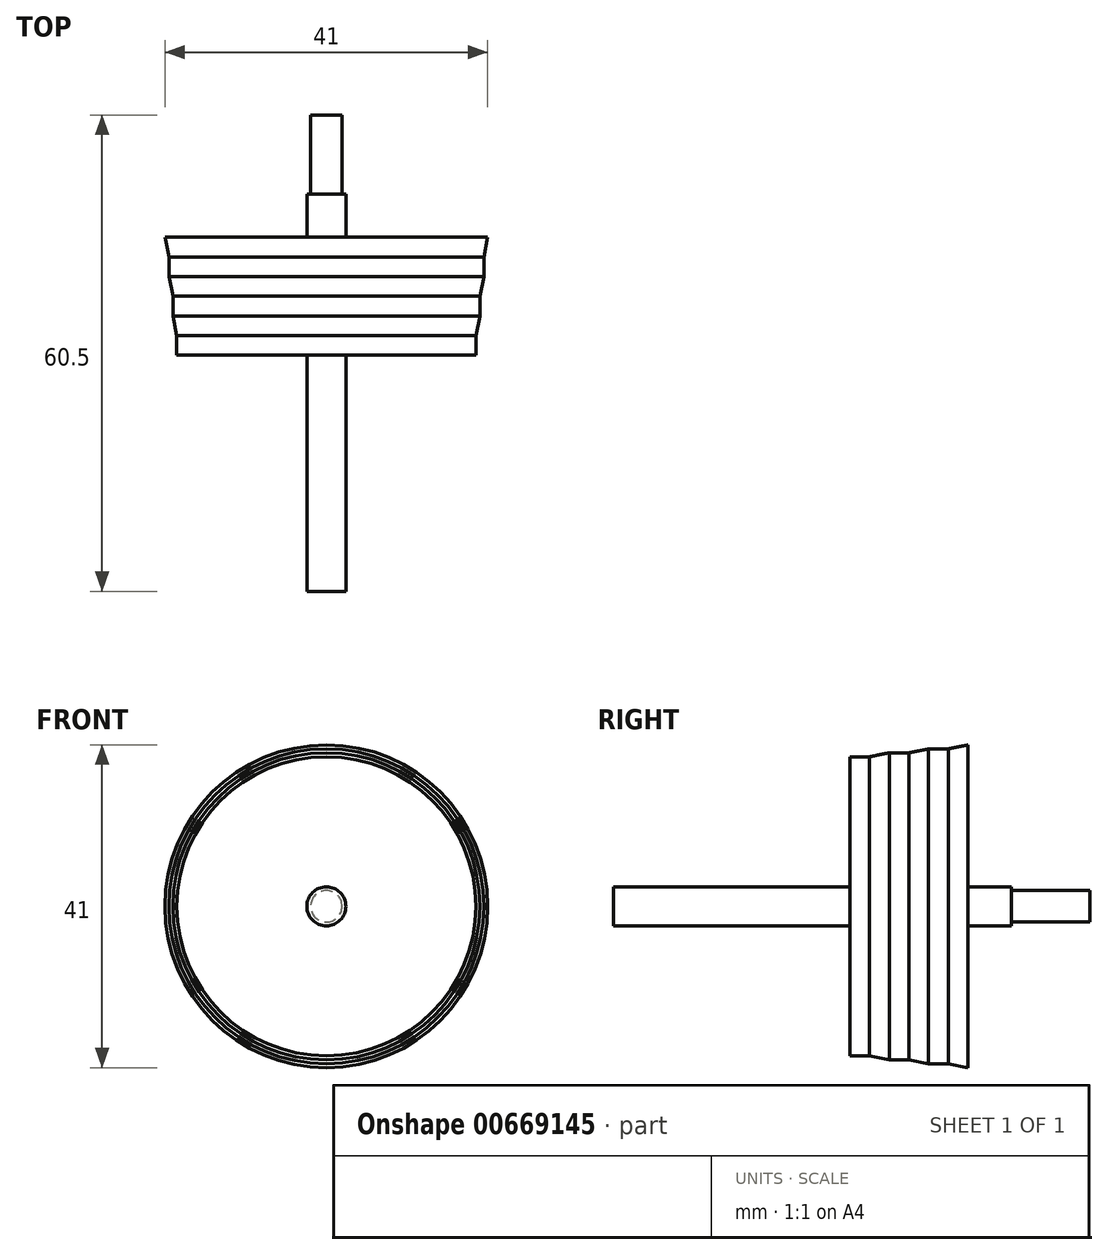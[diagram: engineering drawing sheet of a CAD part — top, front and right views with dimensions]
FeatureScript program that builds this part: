
annotation { "Feature Type Name" : "Feature", "Feature Type Description" : "" }
export const myFeature = defineFeature(function(context is Context, id is Id, definition is map)
    precondition{}
    {
        {
            var Q0;
            Q0=qCreatedBy(makeId("Right.planeOp"),FACE);
            var sketch = newSketch(context, id + "F0", { "sketchPlane" : qUnion([Q0])});
            skLineSegment(sketch, "E0", {"start": v(0, 0) * mm, "end": v(-30, 0) * mm, "construction": true});
            skLineSegment(sketch, "E1", {"start": v(-30, 0) * mm, "end": v(-30, 2.47) * mm});
            skLineSegment(sketch, "E2", {"start": v(-30, 2.48) * mm, "end": v(0, 2.48) * mm});
            skLineSegment(sketch, "E3", {"start": v(0, 2.47) * mm, "end": v(0, 19) * mm});
            skLineSegment(sketch, "E4", {"start": v(0, 19) * mm, "end": v(2.5, 19) * mm});
            skLineSegment(sketch, "E5", {"start": v(2.5, 19) * mm, "end": v(5, 19.5) * mm});
            skLineSegment(sketch, "E6", {"start": v(5, 19.5) * mm, "end": v(7.5, 19.5) * mm});
            skLineSegment(sketch, "E7", {"start": v(7.5, 19.5) * mm, "end": v(10, 20) * mm});
            skLineSegment(sketch, "E8", {"start": v(10, 20) * mm, "end": v(12.5, 20) * mm});
            skLineSegment(sketch, "E9", {"start": v(12.5, 20) * mm, "end": v(15, 20.5) * mm});
            skLineSegment(sketch, "E10", {"start": v(15, 20.5) * mm, "end": v(15, 2.48) * mm});
            skLineSegment(sketch, "E11", {"start": v(15, 2.48) * mm, "end": v(20.5, 2.48) * mm});
            skLineSegment(sketch, "E12", {"start": v(30.5, 0) * mm, "end": v(-30, 0) * mm});
            skLineSegment(sketch, "E13", {"start": v(20.5, 2.48) * mm, "end": v(20.5, 2) * mm});
            skLineSegment(sketch, "E14", {"start": v(20.5, 2) * mm, "end": v(30.5, 2) * mm});
            skLineSegment(sketch, "E15", {"start": v(30.5, 2) * mm, "end": v(30.5, 0) * mm});
            skSolve(sketch);
        }
        {
            var Q0;
            Q0 = qSketchRegion(id + "F0", true);
            var Q1;
            Q1=sQuery(id+"F0.wireOp",EDGE,"E12");
            revolve(context, id + "F1", {"entities" : qUnion([Q0]), "axis" : qUnion([Q1]), "revolveType" : RevolveType.FULL});
        }
    });
